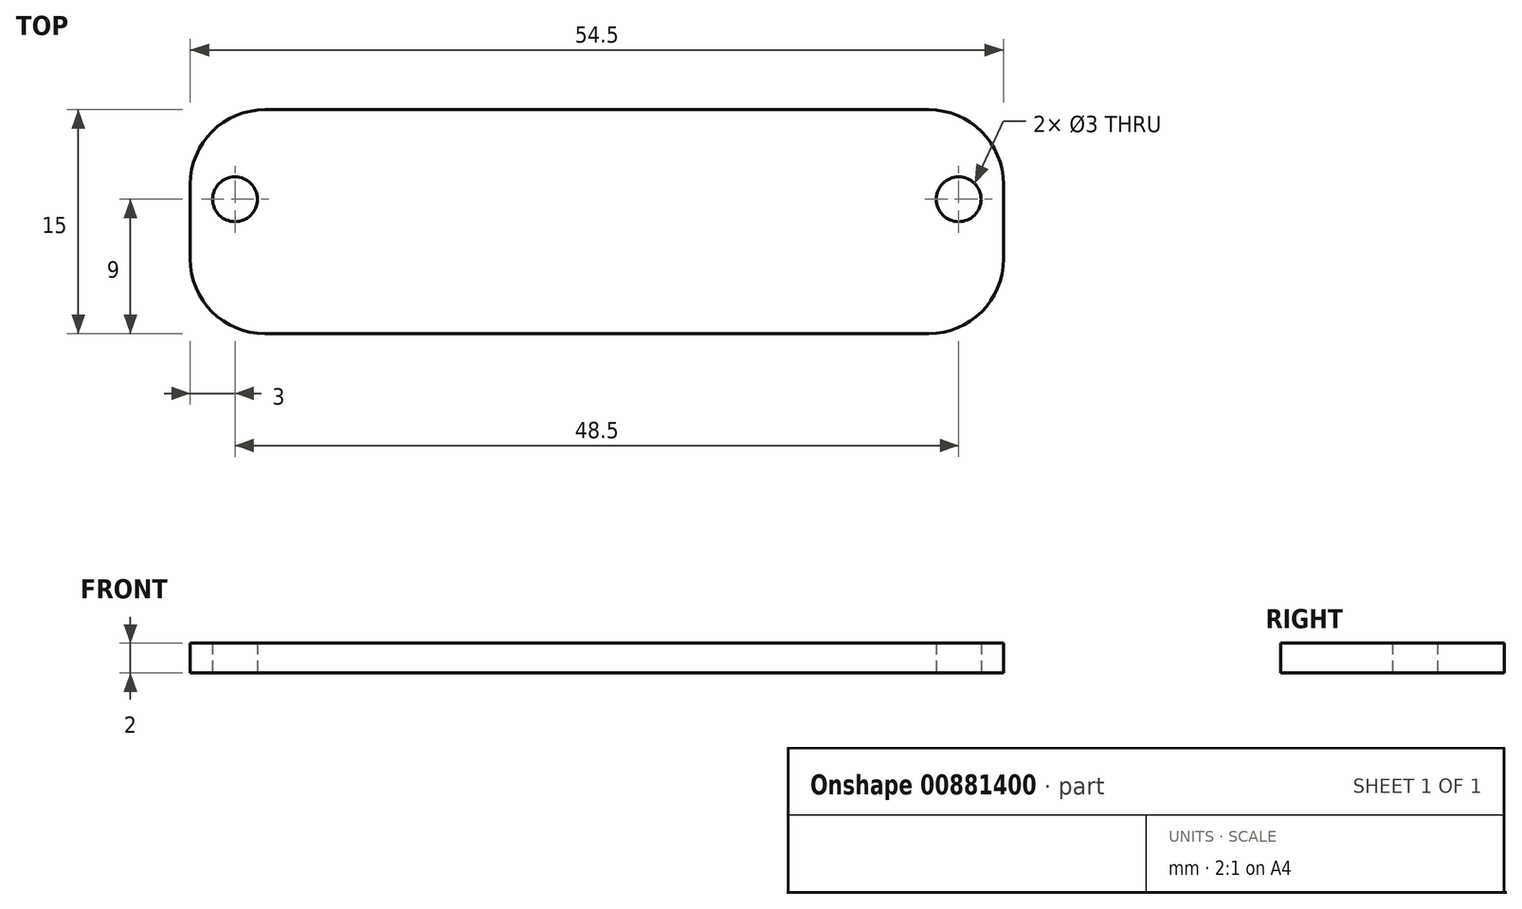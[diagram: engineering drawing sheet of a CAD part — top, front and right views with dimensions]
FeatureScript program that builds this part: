
annotation { "Feature Type Name" : "Feature", "Feature Type Description" : "" }
export const myFeature = defineFeature(function(context is Context, id is Id, definition is map)
    precondition{}
    {
        {
            var Q0;
            Q0=qCreatedBy(makeId("Top.planeOp"),FACE);
            var sketch = newSketch(context, id + "F0", { "sketchPlane" : qUnion([Q0])});
            skLineSegment(sketch, "E0.bottom", {"start": v(33, -7.5) * mm, "end": v(-33, -7.5) * mm});
            skLineSegment(sketch, "E0.top", {"start": v(33, 7.5) * mm, "end": v(-33, 7.5) * mm});
            skLineSegment(sketch, "E0.left", {"start": v(33, -7.5) * mm, "end": v(33, 7.5) * mm});
            skLineSegment(sketch, "E0.right", {"start": v(-33, -7.5) * mm, "end": v(-33, 7.5) * mm});
            skPoint(sketch, "E0.middle", {"position": v(0, 0) * mm});
            skPoint(sketch, "E1", {"position": v(27.25, -7.5) * mm});
            skPoint(sketch, "E2", {"position": v(-27.25, -7.5) * mm});
            skPoint(sketch, "E3", {"position": v(-27.25, -22.5) * mm});
            skPoint(sketch, "E4", {"position": v(27.25, -22.5) * mm});
            skLineSegment(sketch, "E5", {"start": v(-27.25, -7.5) * mm, "end": v(-27.25, -22.5) * mm});
            skLineSegment(sketch, "E6", {"start": v(-27.25, -22.5) * mm, "end": v(27.25, -22.5) * mm});
            skLineSegment(sketch, "E7", {"start": v(27.25, -22.5) * mm, "end": v(27.25, -7.5) * mm});
            skPoint(sketch, "E8", {"position": v(-30, -3.5) * mm});
            skPoint(sketch, "E9", {"position": v(30, -3.5) * mm});
            skPoint(sketch, "E10", {"position": v(-24.25, -13.5) * mm});
            skPoint(sketch, "E11", {"position": v(24.25, -13.5) * mm});
            skCircle(sketch, "E12", {"center": v(-30, -3.5) * mm, "radius": 1.5 * mm});
            skCircle(sketch, "E13", {"center": v(30, -3.5) * mm, "radius": 1.5 * mm});
            skCircle(sketch, "E14", {"center": v(-24.25, -13.5) * mm, "radius": 1.5 * mm});
            skCircle(sketch, "E15", {"center": v(24.25, -13.5) * mm, "radius": 1.5 * mm});
            skSolve(sketch);
        }
        {
            var Q0;
            Q0=makeQuery(id+"F0.imprint","IMPRINT",FACE,{"disambiguationData":[TD([[makeQuery(id+"F0.imprint","IMPRINT",EDGE,{"derivedFrom":sQuery(id+"F0.wireOp",EDGE,"E0.top")}),1.0]])]});
            var Q1;
            {var subQ1=sQuery(id+"F0.wireOp",EDGE,"E5");Q1=makeQuery(id+"F0.imprint","IMPRINT",FACE,{"disambiguationData":[TD([[makeQuery(id+"F0.imprint","IMPRINT",EDGE,{"derivedFrom":subQ1}),1.0]])]});}
            extrude(context, id + "F1", {"entities" : qUnion([Q0, Q1]), "depth" : 2 * mm, "offsetDistance" : 25 * mm});
        }
        {
            var Q0;
            Q0=makeQuery(id+"F1.opExtrude","SWEPT_EDGE",EDGE,{"disambiguationData":[OSD([sQuery(id+"F0.wireOp",EDGE,"E0.top"),sQuery(id+"F0.wireOp",EDGE,"E0.right")])]});
            var Q1;
            Q1=makeQuery(id+"F1.opExtrude","SWEPT_EDGE",EDGE,{"disambiguationData":[OSD([sQuery(id+"F0.wireOp",EDGE,"E0.top"),sQuery(id+"F0.wireOp",EDGE,"E0.left")])]});
            var Q2;
            Q2=makeQuery(id+"F1.opExtrude","SWEPT_EDGE",EDGE,{"disambiguationData":[OSD([sQuery(id+"F0.wireOp",EDGE,"E6"),sQuery(id+"F0.wireOp",EDGE,"E7")])]});
            var Q3;
            Q3=makeQuery(id+"F1.opExtrude","SWEPT_EDGE",EDGE,{"disambiguationData":[OSD([sQuery(id+"F0.wireOp",EDGE,"E5"),sQuery(id+"F0.wireOp",EDGE,"E6")])]});
            var Q4;
            Q4=makeQuery(id+"F1.opExtrude","SWEPT_EDGE",EDGE,{"disambiguationData":[OSD([sQuery(id+"F0.wireOp",EDGE,"E0.bottom"),sQuery(id+"F0.wireOp",EDGE,"E0.left")])]});
            var Q5;
            Q5=makeQuery(id+"F1.opExtrude","SWEPT_EDGE",EDGE,{"disambiguationData":[OSD([sQuery(id+"F0.wireOp",EDGE,"E0.bottom"),sQuery(id+"F0.wireOp",EDGE,"E0.right")])]});
            fillet(context, id + "F2", {"entities" : qUnion([Q0, Q1, Q2, Q3, Q4, Q5]), "tangentPropagation" : true, "radius" : 5 * mm, "defaultsChanged" : false, "vertexSettings" : [], "allowEdgeOverflow" : false});
        }
    });
